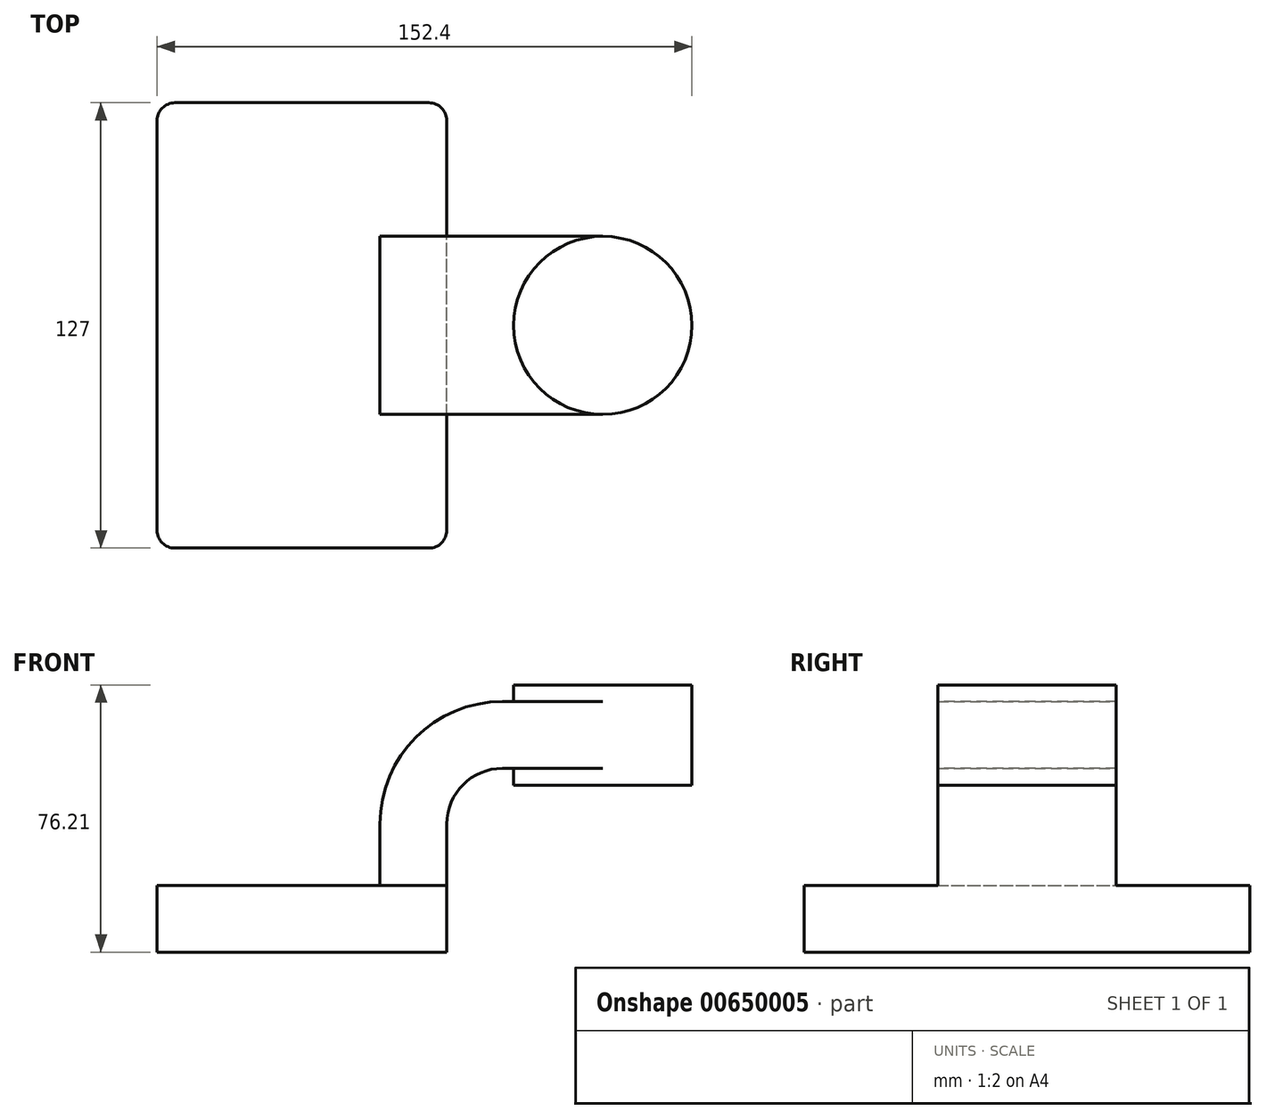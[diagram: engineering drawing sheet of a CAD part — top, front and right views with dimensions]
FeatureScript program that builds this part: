
annotation { "Feature Type Name" : "Feature", "Feature Type Description" : "" }
export const myFeature = defineFeature(function(context is Context, id is Id, definition is map)
    precondition{}
    {
        {
            var Q0;
            Q0=qCreatedBy(makeId("Front.planeOp"),FACE);
            var sketch = newSketch(context, id + "F0", { "sketchPlane" : qUnion([Q0])});
            skLineSegment(sketch, "E0.bottom", {"start": v(-41.28, 9.52) * mm, "end": v(41.27, 9.53) * mm});
            skLineSegment(sketch, "E0.top", {"start": v(-41.28, -9.53) * mm, "end": v(41.28, -9.53) * mm});
            skLineSegment(sketch, "E0.left", {"start": v(-41.28, 9.52) * mm, "end": v(-41.27, -9.53) * mm});
            skLineSegment(sketch, "E0.right", {"start": v(41.28, 9.53) * mm, "end": v(41.28, -9.52) * mm});
            skPoint(sketch, "E0.middle", {"position": v(0, 0) * mm});
            skLineSegment(sketch, "E1.bottom", {"start": v(60.32, 38.1) * mm, "end": v(111.12, 38.1) * mm});
            skLineSegment(sketch, "E1.top", {"start": v(60.32, 66.68) * mm, "end": v(111.12, 66.68) * mm});
            skLineSegment(sketch, "E1.left", {"start": v(60.32, 38.1) * mm, "end": v(60.32, 66.68) * mm});
            skLineSegment(sketch, "E1.right", {"start": v(111.12, 38.1) * mm, "end": v(111.12, 66.68) * mm});
            skPoint(sketch, "E1.middle", {"position": v(85.72, 52.39) * mm});
            skLineSegment(sketch, "E2", {"start": v(41.27, 9.53) * mm, "end": v(41.27, 27) * mm});
            skArc(sketch, "E3", {"start": v(41.27, 27) * mm, "mid": v(45.92, 38.23) * mm, "end": v(57.15, 42.88) * mm});
            skLineSegment(sketch, "E4", {"start": v(57.15, 42.88) * mm, "end": v(85.72, 42.88) * mm});
            skLineSegment(sketch, "E5.0", {"start": v(57.15, 61.93) * mm, "end": v(85.72, 61.93) * mm});
            skArc(sketch, "E5.1", {"start": v(22.23, 27) * mm, "mid": v(32.45, 51.7) * mm, "end": v(57.15, 61.93) * mm});
            skLineSegment(sketch, "E5.2", {"start": v(22.22, 9.53) * mm, "end": v(22.22, 27) * mm});
            skFitSpline(sketch, "E6", {"points": [v(-41.28, 9.53) * mm, v(57.15, 61.93) * mm], "startDerivative": vector(6.25, 65) * mm, "endDerivative": vector(133.17, -2.78) * mm});
            skLineSegment(sketch, "E7", {"start": v(85.72, 66.68) * mm, "end": v(85.72, 38.1) * mm});
            skSolve(sketch);
        }
        {
            var Q0;
            Q0=makeQuery(id+"F0.imprint","IMPRINT",FACE,{"disambiguationData":[TD([[makeQuery(id+"F0.imprint","IMPRINT",EDGE,{"derivedFrom":sQuery(id+"F0.wireOp",EDGE,"E0.top")}),1.0]])]});
            extrude(context, id + "F1", {"entities" : qUnion([Q0]), "endBound" : BoundingType.SYMMETRIC, "depth" : 127 * mm, "offsetDistance" : 25.4 * mm});
        }
        {
            var Q0;
            {var subQ1=sQuery(id+"F0.wireOp",EDGE,"E2");Q0=makeQuery(id+"F0.imprint","IMPRINT",FACE,{"disambiguationData":[TD([[makeQuery(id+"F0.imprint","IMPRINT",EDGE,{"derivedFrom":subQ1}),1.0]])]});}
            var Q1;
            {var subQ5=sQuery(id+"F0.wireOp",EDGE,"ajkGCxn2-Ot74-KxLS-hKuB-NWpmFdrcsQCW");Q1=makeQuery(id+"F0.imprint","IMPRINT",FACE,{"disambiguationData":[TD([[makeQuery(id+"F0.imprint","IMPRINT",EDGE,{"derivedFrom":subQ5}),1.0]])]});}
            extrude(context, id + "F2", {"entities" : qUnion([Q0, Q1]), "operationType" : NewBodyOperationType.ADD, "endBound" : BoundingType.SYMMETRIC, "depth" : 50.8 * mm, "offsetDistance" : 25.4 * mm});
        }
        {
            var Q0;
            Q0=makeQuery(id+"F0.imprint","IMPRINT",FACE,{"disambiguationData":[TD([[makeQuery(id+"F0.imprint","IMPRINT",EDGE,{"derivedFrom":sQuery(id+"F0.wireOp",EDGE,"E5.1")}),1.0]])]});
            extrude(context, id + "F3", {"entities" : qUnion([Q0]), "operationType" : NewBodyOperationType.ADD, "endBound" : BoundingType.SYMMETRIC, "depth" : 15.88 * mm, "offsetDistance" : 25.4 * mm});
        }
        {
            var Q0;
            {var subQ0=sQuery(id+"F0.wireOp",EDGE,"E4");var subQ1=sQuery(id+"F0.wireOp",EDGE,"E1.left");var subQ2=makeQuery(id+"F0.imprint","INTERSECT",VERTEX,{"derivedFrom":[subQ1,subQ0]});Q0=makeQuery(id+"F0.imprint","IMPRINT",FACE,{"disambiguationData":[TD([[makeQuery(id+"F0.imprint","IMPRINT",EDGE,{"disambiguationData":[TD([[subQ2,-1.0]])],"derivedFrom":subQ1}),-1.0]])]});}
            extrude(context, id + "F4", {"entities" : qUnion([Q0]), "operationType" : NewBodyOperationType.ADD, "endBound" : BoundingType.SYMMETRIC, "depth" : 50.8 * mm, "offsetDistance" : 25.4 * mm});
        }
        {
            var Q0;
            {var subQ4=sQuery(id+"F0.wireOp",EDGE,"E1.right");Q0=makeQuery(id+"F0.imprint","IMPRINT",FACE,{"disambiguationData":[TD([[makeQuery(id+"F0.imprint","IMPRINT",EDGE,{"derivedFrom":subQ4}),1.0]])]});}
            var Q1;
            Q1=sQuery(id+"F0.wireOp",EDGE,"E7");
            revolve(context, id + "F5", {"operationType" : NewBodyOperationType.ADD, "entities" : qUnion([Q0]), "axis" : qUnion([Q1]), "revolveType" : RevolveType.FULL});
        }
        {
            var Q0;
            Q0=makeQuery(id+"F1.opExtrude","CAP_EDGE",EDGE,{"disambiguationData":[OSD([sQuery(id+"F0.wireOp",EDGE,"E0.right")])],"isStart":false});
            var Q1;
            Q1=makeQuery(id+"F1.opExtrude","CAP_EDGE",EDGE,{"disambiguationData":[OSD([sQuery(id+"F0.wireOp",EDGE,"E0.left")])],"isStart":false});
            var Q2;
            Q2=makeQuery(id+"F1.opExtrude","CAP_EDGE",EDGE,{"disambiguationData":[OSD([sQuery(id+"F0.wireOp",EDGE,"E0.left")])],"isStart":true});
            var Q3;
            Q3=makeQuery(id+"F1.opExtrude","CAP_EDGE",EDGE,{"disambiguationData":[OSD([sQuery(id+"F0.wireOp",EDGE,"E0.right")])],"isStart":true});
            fillet(context, id + "F6", {"entities" : qUnion([Q0, Q1, Q2, Q3]), "radius" : 5.08 * mm, "tangentPropagation" : true, "allowEdgeOverflow" : false});
        }
    });
